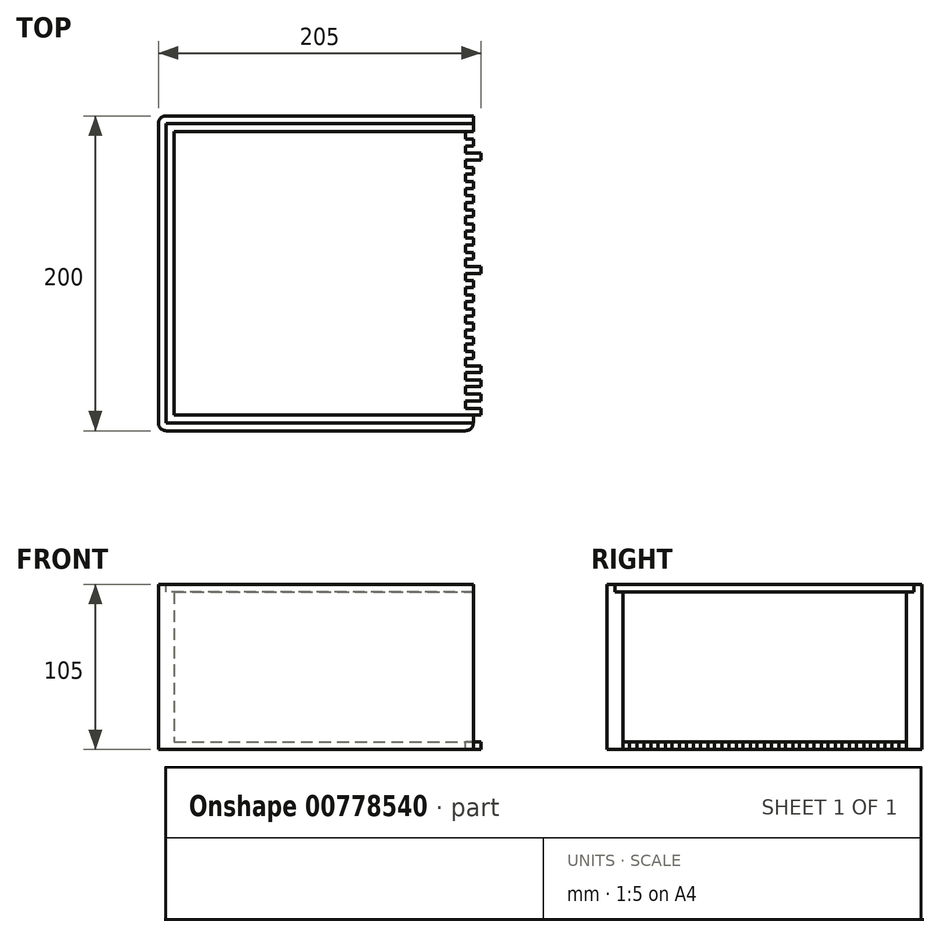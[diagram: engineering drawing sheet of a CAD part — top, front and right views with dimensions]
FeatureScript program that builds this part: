
annotation { "Feature Type Name" : "Feature", "Feature Type Description" : "" }
export const myFeature = defineFeature(function(context is Context, id is Id, definition is map)
    precondition{}
    {
        {
            var Q0;
            Q0=qCreatedBy(makeId("Top.planeOp"),FACE);
            var sketch = newSketch(context, id + "F0", { "sketchPlane" : qUnion([Q0])});
            skLineSegment(sketch, "E0.bottom", {"start": v(100, -100) * mm, "end": v(-100, -100) * mm});
            skLineSegment(sketch, "E0.top", {"start": v(100, 100) * mm, "end": v(-100, 100) * mm});
            skLineSegment(sketch, "E0.left", {"start": v(100, -100) * mm, "end": v(100, 100) * mm});
            skLineSegment(sketch, "E0.right", {"start": v(-100, -100) * mm, "end": v(-100, 100) * mm});
            skPoint(sketch, "E0.middle", {"position": v(0, 0) * mm});
            skSolve(sketch);
        }
        {
            var Q0;
            Q0 = qSketchRegion(id + "F0", true);
            extrude(context, id + "F1", {"entities" : qUnion([Q0]), "depth" : 5 * mm, "offsetDistance" : 25 * mm});
        }
        {
            var Q0;
            Q0=makeQuery(id+"F1.opExtrude","CAP_FACE",FACE,{"disambiguationData":[OSD([sQuery(id+"F0.wireOp",EDGE,"E0.bottom"),sQuery(id+"F0.wireOp",EDGE,"E0.top"),sQuery(id+"F0.wireOp",EDGE,"E0.left"),sQuery(id+"F0.wireOp",EDGE,"E0.right")])],"isStart":false});
            var sketch = newSketch(context, id + "F2", { "sketchPlane" : qUnion([Q0])});
            skLineSegment(sketch, "E1.bottom", {"start": v(-100, 100) * mm, "end": v(100, 100) * mm});
            skLineSegment(sketch, "E1.top", {"start": v(-100, 90) * mm, "end": v(100, 90) * mm});
            skLineSegment(sketch, "E1.left", {"start": v(-100, 100) * mm, "end": v(-100, 90) * mm});
            skLineSegment(sketch, "E1.right", {"start": v(100, 100) * mm, "end": v(100, 90) * mm});
            skLineSegment(sketch, "E2.bottom", {"start": v(-100, 100) * mm, "end": v(-90, 100) * mm});
            skLineSegment(sketch, "E2.top", {"start": v(-100, -100) * mm, "end": v(-90, -100) * mm});
            skLineSegment(sketch, "E2.left", {"start": v(-100, 100) * mm, "end": v(-100, -100) * mm});
            skLineSegment(sketch, "E2.right", {"start": v(-90, 100) * mm, "end": v(-90, -100) * mm});
            skLineSegment(sketch, "E3.bottom", {"start": v(-100, -100) * mm, "end": v(100, -100) * mm});
            skLineSegment(sketch, "E3.top", {"start": v(-100, -90) * mm, "end": v(100, -90) * mm});
            skLineSegment(sketch, "E3.left", {"start": v(-100, -100) * mm, "end": v(-100, -90) * mm});
            skLineSegment(sketch, "E3.right", {"start": v(100, -100) * mm, "end": v(100, -90) * mm});
            skSolve(sketch);
        }
        {
            var Q0;
            Q0 = qSketchRegion(id + "F2", true);
            extrude(context, id + "F3", {"entities" : qUnion([Q0]), "operationType" : NewBodyOperationType.ADD, "depth" : 100 * mm, "offsetDistance" : 25 * mm});
        }
        {
            var Q0;
            Q0=makeQuery(id+"F3.opExtrude","CAP_FACE",FACE,{"disambiguationData":[OSD([sQuery(id+"F2.wireOp",EDGE,"E1.bottom"),sQuery(id+"F2.wireOp",EDGE,"E1.top"),sQuery(id+"F2.wireOp",EDGE,"E1.right"),sQuery(id+"F2.wireOp",EDGE,"E2.bottom"),sQuery(id+"F2.wireOp",EDGE,"E2.left"),sQuery(id+"F2.wireOp",EDGE,"E2.right"),sQuery(id+"F2.wireOp",EDGE,"E3.bottom"),sQuery(id+"F2.wireOp",EDGE,"E3.top"),sQuery(id+"F2.wireOp",EDGE,"E3.left"),sQuery(id+"F2.wireOp",EDGE,"E3.right")])],"isStart":false});
            var sketch = newSketch(context, id + "F4", { "sketchPlane" : qUnion([Q0])});
            skLineSegment(sketch, "E4", {"start": v(100, 95) * mm, "end": v(-95, 95) * mm});
            skLineSegment(sketch, "E5", {"start": v(-95, 95) * mm, "end": v(-95, -95) * mm});
            skLineSegment(sketch, "E6", {"start": v(-95, -95) * mm, "end": v(100, -95) * mm});
            skSolve(sketch);
        }
        {
            var Q0;
            {var subQ4=sQuery(id+"F4.wireOp",EDGE,"E4");Q0=makeQuery(id+"F4.imprint","IMPRINT",FACE,{"disambiguationData":[TD([[makeQuery(id+"F4.imprint","IMPRINT",EDGE,{"derivedFrom":subQ4}),1.0]])]});}
            extrude(context, id + "F5", {"entities" : qUnion([Q0]), "operationType" : NewBodyOperationType.REMOVE, "oppositeDirection" : true, "depth" : 5 * mm, "offsetDistance" : 25 * mm});
        }
        {
            var Q0;
            Q0=makeQuery(id+"F1.opExtrude","CAP_FACE",FACE,{"disambiguationData":[OSD([sQuery(id+"F0.wireOp",EDGE,"E0.bottom"),sQuery(id+"F0.wireOp",EDGE,"E0.top"),sQuery(id+"F0.wireOp",EDGE,"E0.left"),sQuery(id+"F0.wireOp",EDGE,"E0.right")])],"isStart":false});
            var sketch = newSketch(context, id + "F6", { "sketchPlane" : qUnion([Q0])});
            skLineSegment(sketch, "E7", {"start": v(100, -90) * mm, "end": v(100, 90) * mm});
            skLineSegment(sketch, "E8.bottom", {"start": v(100, -90) * mm, "end": v(95, -90) * mm});
            skLineSegment(sketch, "E8.top", {"start": v(100, -85.7) * mm, "end": v(95, -85.7) * mm});
            skLineSegment(sketch, "E8.left", {"start": v(100, -90) * mm, "end": v(100, -85.7) * mm});
            skLineSegment(sketch, "E8.right", {"start": v(95, -90) * mm, "end": v(95, -85.7) * mm});
            skLineSegment(sketch, "E9.top", {"start": v(100, -81) * mm, "end": v(95, -81) * mm});
            skLineSegment(sketch, "E9.left", {"start": v(100, -85.7) * mm, "end": v(100, -81) * mm});
            skLineSegment(sketch, "E9.right", {"start": v(95, -85.7) * mm, "end": v(95, -81) * mm});
            skLineSegment(sketch, "E10.0.1.0", {"start": v(95, -81) * mm, "end": v(95, -76.7) * mm});
            skLineSegment(sketch, "E10.0.1.1", {"start": v(100, -81) * mm, "end": v(100, -76.7) * mm});
            skLineSegment(sketch, "E10.0.1.2", {"start": v(100, -76.7) * mm, "end": v(100, -72) * mm});
            skLineSegment(sketch, "E10.0.1.3", {"start": v(95, -76.7) * mm, "end": v(95, -72) * mm});
            skLineSegment(sketch, "E10.0.1.4", {"start": v(100, -76.7) * mm, "end": v(95, -76.7) * mm});
            skLineSegment(sketch, "E10.0.1.5", {"start": v(100, -72) * mm, "end": v(95, -72) * mm});
            skLineSegment(sketch, "E10.0.2.0", {"start": v(95, -72) * mm, "end": v(95, -67.7) * mm});
            skLineSegment(sketch, "E10.0.2.1", {"start": v(100, -72) * mm, "end": v(100, -67.7) * mm});
            skLineSegment(sketch, "E10.0.2.2", {"start": v(100, -67.7) * mm, "end": v(100, -63) * mm});
            skLineSegment(sketch, "E10.0.2.3", {"start": v(95, -67.7) * mm, "end": v(95, -63) * mm});
            skLineSegment(sketch, "E10.0.2.4", {"start": v(100, -67.7) * mm, "end": v(95, -67.7) * mm});
            skLineSegment(sketch, "E10.0.2.5", {"start": v(100, -63) * mm, "end": v(95, -63) * mm});
            skLineSegment(sketch, "E10.0.3.0", {"start": v(95, -63) * mm, "end": v(95, -58.7) * mm});
            skLineSegment(sketch, "E10.0.3.1", {"start": v(100, -63) * mm, "end": v(100, -58.7) * mm});
            skLineSegment(sketch, "E10.0.3.2", {"start": v(100, -58.7) * mm, "end": v(100, -54) * mm});
            skLineSegment(sketch, "E10.0.3.3", {"start": v(95, -58.7) * mm, "end": v(95, -54) * mm});
            skLineSegment(sketch, "E10.0.3.4", {"start": v(100, -58.7) * mm, "end": v(95, -58.7) * mm});
            skLineSegment(sketch, "E10.0.3.5", {"start": v(100, -54) * mm, "end": v(95, -54) * mm});
            skLineSegment(sketch, "E10.0.4.0", {"start": v(95, -54) * mm, "end": v(95, -49.7) * mm});
            skLineSegment(sketch, "E10.0.4.1", {"start": v(100, -54) * mm, "end": v(100, -49.7) * mm});
            skLineSegment(sketch, "E10.0.4.2", {"start": v(100, -49.7) * mm, "end": v(100, -45) * mm});
            skLineSegment(sketch, "E10.0.4.3", {"start": v(95, -49.7) * mm, "end": v(95, -45) * mm});
            skLineSegment(sketch, "E10.0.4.4", {"start": v(100, -49.7) * mm, "end": v(95, -49.7) * mm});
            skLineSegment(sketch, "E10.0.4.5", {"start": v(100, -45) * mm, "end": v(95, -45) * mm});
            skLineSegment(sketch, "E10.0.5.0", {"start": v(95, -45) * mm, "end": v(95, -40.7) * mm});
            skLineSegment(sketch, "E10.0.5.1", {"start": v(100, -45) * mm, "end": v(100, -40.7) * mm});
            skLineSegment(sketch, "E10.0.5.2", {"start": v(100, -40.7) * mm, "end": v(100, -36) * mm});
            skLineSegment(sketch, "E10.0.5.3", {"start": v(95, -40.7) * mm, "end": v(95, -36) * mm});
            skLineSegment(sketch, "E10.0.5.4", {"start": v(100, -40.7) * mm, "end": v(95, -40.7) * mm});
            skLineSegment(sketch, "E10.0.5.5", {"start": v(100, -36) * mm, "end": v(95, -36) * mm});
            skLineSegment(sketch, "E10.0.6.0", {"start": v(95, -36) * mm, "end": v(95, -31.7) * mm});
            skLineSegment(sketch, "E10.0.6.1", {"start": v(100, -36) * mm, "end": v(100, -31.7) * mm});
            skLineSegment(sketch, "E10.0.6.2", {"start": v(100, -31.7) * mm, "end": v(100, -27) * mm});
            skLineSegment(sketch, "E10.0.6.3", {"start": v(95, -31.7) * mm, "end": v(95, -27) * mm});
            skLineSegment(sketch, "E10.0.6.4", {"start": v(100, -31.7) * mm, "end": v(95, -31.7) * mm});
            skLineSegment(sketch, "E10.0.6.5", {"start": v(100, -27) * mm, "end": v(95, -27) * mm});
            skLineSegment(sketch, "E10.0.7.0", {"start": v(95, -27) * mm, "end": v(95, -22.7) * mm});
            skLineSegment(sketch, "E10.0.7.1", {"start": v(100, -27) * mm, "end": v(100, -22.7) * mm});
            skLineSegment(sketch, "E10.0.7.2", {"start": v(100, -22.7) * mm, "end": v(100, -18) * mm});
            skLineSegment(sketch, "E10.0.7.3", {"start": v(95, -22.7) * mm, "end": v(95, -18) * mm});
            skLineSegment(sketch, "E10.0.7.4", {"start": v(100, -22.7) * mm, "end": v(95, -22.7) * mm});
            skLineSegment(sketch, "E10.0.7.5", {"start": v(100, -18) * mm, "end": v(95, -18) * mm});
            skLineSegment(sketch, "E10.0.8.0", {"start": v(95, -18) * mm, "end": v(95, -13.7) * mm});
            skLineSegment(sketch, "E10.0.8.1", {"start": v(100, -18) * mm, "end": v(100, -13.7) * mm});
            skLineSegment(sketch, "E10.0.8.2", {"start": v(100, -13.7) * mm, "end": v(100, -9) * mm});
            skLineSegment(sketch, "E10.0.8.3", {"start": v(95, -13.7) * mm, "end": v(95, -9) * mm});
            skLineSegment(sketch, "E10.0.8.4", {"start": v(100, -13.7) * mm, "end": v(95, -13.7) * mm});
            skLineSegment(sketch, "E10.0.8.5", {"start": v(100, -9) * mm, "end": v(95, -9) * mm});
            skLineSegment(sketch, "E10.0.9.0", {"start": v(95, -9) * mm, "end": v(95, -4.7) * mm});
            skLineSegment(sketch, "E10.0.9.1", {"start": v(100, -9) * mm, "end": v(100, -4.7) * mm});
            skLineSegment(sketch, "E10.0.9.2", {"start": v(100, -4.7) * mm, "end": v(100, 0) * mm});
            skLineSegment(sketch, "E10.0.9.3", {"start": v(95, -4.7) * mm, "end": v(95, 0) * mm});
            skLineSegment(sketch, "E10.0.9.4", {"start": v(100, -4.7) * mm, "end": v(95, -4.7) * mm});
            skLineSegment(sketch, "E10.0.9.5", {"start": v(100, 0) * mm, "end": v(95, 0) * mm});
            skLineSegment(sketch, "E10.0.10.0", {"start": v(95, 0) * mm, "end": v(95, 4.3) * mm});
            skLineSegment(sketch, "E10.0.10.1", {"start": v(100, 0) * mm, "end": v(100, 4.3) * mm});
            skLineSegment(sketch, "E10.0.10.2", {"start": v(100, 4.3) * mm, "end": v(100, 9) * mm});
            skLineSegment(sketch, "E10.0.10.3", {"start": v(95, 4.3) * mm, "end": v(95, 9) * mm});
            skLineSegment(sketch, "E10.0.10.4", {"start": v(100, 4.3) * mm, "end": v(95, 4.3) * mm});
            skLineSegment(sketch, "E10.0.10.5", {"start": v(100, 9) * mm, "end": v(95, 9) * mm});
            skLineSegment(sketch, "E10.0.11.0", {"start": v(95, 9) * mm, "end": v(95, 13.3) * mm});
            skLineSegment(sketch, "E10.0.11.1", {"start": v(100, 9) * mm, "end": v(100, 13.3) * mm});
            skLineSegment(sketch, "E10.0.11.2", {"start": v(100, 13.3) * mm, "end": v(100, 18) * mm});
            skLineSegment(sketch, "E10.0.11.3", {"start": v(95, 13.3) * mm, "end": v(95, 18) * mm});
            skLineSegment(sketch, "E10.0.11.4", {"start": v(100, 13.3) * mm, "end": v(95, 13.3) * mm});
            skLineSegment(sketch, "E10.0.11.5", {"start": v(100, 18) * mm, "end": v(95, 18) * mm});
            skLineSegment(sketch, "E10.0.12.0", {"start": v(95, 18) * mm, "end": v(95, 22.3) * mm});
            skLineSegment(sketch, "E10.0.12.1", {"start": v(100, 18) * mm, "end": v(100, 22.3) * mm});
            skLineSegment(sketch, "E10.0.12.2", {"start": v(100, 22.3) * mm, "end": v(100, 27) * mm});
            skLineSegment(sketch, "E10.0.12.3", {"start": v(95, 22.3) * mm, "end": v(95, 27) * mm});
            skLineSegment(sketch, "E10.0.12.4", {"start": v(100, 22.3) * mm, "end": v(95, 22.3) * mm});
            skLineSegment(sketch, "E10.0.12.5", {"start": v(100, 27) * mm, "end": v(95, 27) * mm});
            skLineSegment(sketch, "E10.0.13.0", {"start": v(95, 27) * mm, "end": v(95, 31.3) * mm});
            skLineSegment(sketch, "E10.0.13.1", {"start": v(100, 27) * mm, "end": v(100, 31.3) * mm});
            skLineSegment(sketch, "E10.0.13.2", {"start": v(100, 31.3) * mm, "end": v(100, 36) * mm});
            skLineSegment(sketch, "E10.0.13.3", {"start": v(95, 31.3) * mm, "end": v(95, 36) * mm});
            skLineSegment(sketch, "E10.0.13.4", {"start": v(100, 31.3) * mm, "end": v(95, 31.3) * mm});
            skLineSegment(sketch, "E10.0.13.5", {"start": v(100, 36) * mm, "end": v(95, 36) * mm});
            skLineSegment(sketch, "E10.0.14.0", {"start": v(95, 36) * mm, "end": v(95, 40.3) * mm});
            skLineSegment(sketch, "E10.0.14.1", {"start": v(100, 36) * mm, "end": v(100, 40.3) * mm});
            skLineSegment(sketch, "E10.0.14.2", {"start": v(100, 40.3) * mm, "end": v(100, 45) * mm});
            skLineSegment(sketch, "E10.0.14.3", {"start": v(95, 40.3) * mm, "end": v(95, 45) * mm});
            skLineSegment(sketch, "E10.0.14.4", {"start": v(100, 40.3) * mm, "end": v(95, 40.3) * mm});
            skLineSegment(sketch, "E10.0.14.5", {"start": v(100, 45) * mm, "end": v(95, 45) * mm});
            skLineSegment(sketch, "E10.0.15.0", {"start": v(95, 45) * mm, "end": v(95, 49.3) * mm});
            skLineSegment(sketch, "E10.0.15.1", {"start": v(100, 45) * mm, "end": v(100, 49.3) * mm});
            skLineSegment(sketch, "E10.0.15.2", {"start": v(100, 49.3) * mm, "end": v(100, 54) * mm});
            skLineSegment(sketch, "E10.0.15.3", {"start": v(95, 49.3) * mm, "end": v(95, 54) * mm});
            skLineSegment(sketch, "E10.0.15.4", {"start": v(100, 49.3) * mm, "end": v(95, 49.3) * mm});
            skLineSegment(sketch, "E10.0.15.5", {"start": v(100, 54) * mm, "end": v(95, 54) * mm});
            skLineSegment(sketch, "E10.0.16.0", {"start": v(95, 54) * mm, "end": v(95, 58.3) * mm});
            skLineSegment(sketch, "E10.0.16.1", {"start": v(100, 54) * mm, "end": v(100, 58.3) * mm});
            skLineSegment(sketch, "E10.0.16.2", {"start": v(100, 58.3) * mm, "end": v(100, 63) * mm});
            skLineSegment(sketch, "E10.0.16.3", {"start": v(95, 58.3) * mm, "end": v(95, 63) * mm});
            skLineSegment(sketch, "E10.0.16.4", {"start": v(100, 58.3) * mm, "end": v(95, 58.3) * mm});
            skLineSegment(sketch, "E10.0.16.5", {"start": v(100, 63) * mm, "end": v(95, 63) * mm});
            skLineSegment(sketch, "E10.0.17.0", {"start": v(95, 63) * mm, "end": v(95, 67.3) * mm});
            skLineSegment(sketch, "E10.0.17.1", {"start": v(100, 63) * mm, "end": v(100, 67.3) * mm});
            skLineSegment(sketch, "E10.0.17.2", {"start": v(100, 67.3) * mm, "end": v(100, 72) * mm});
            skLineSegment(sketch, "E10.0.17.3", {"start": v(95, 67.3) * mm, "end": v(95, 72) * mm});
            skLineSegment(sketch, "E10.0.17.4", {"start": v(100, 67.3) * mm, "end": v(95, 67.3) * mm});
            skLineSegment(sketch, "E10.0.17.5", {"start": v(100, 72) * mm, "end": v(95, 72) * mm});
            skLineSegment(sketch, "E10.0.18.0", {"start": v(95, 72) * mm, "end": v(95, 76.3) * mm});
            skLineSegment(sketch, "E10.0.18.1", {"start": v(100, 72) * mm, "end": v(100, 76.3) * mm});
            skLineSegment(sketch, "E10.0.18.2", {"start": v(100, 76.3) * mm, "end": v(100, 81) * mm});
            skLineSegment(sketch, "E10.0.18.3", {"start": v(95, 76.3) * mm, "end": v(95, 81) * mm});
            skLineSegment(sketch, "E10.0.18.4", {"start": v(100, 76.3) * mm, "end": v(95, 76.3) * mm});
            skLineSegment(sketch, "E10.0.18.5", {"start": v(100, 81) * mm, "end": v(95, 81) * mm});
            skLineSegment(sketch, "E10.0.19.0", {"start": v(95, 81) * mm, "end": v(95, 85.3) * mm});
            skLineSegment(sketch, "E10.0.19.1", {"start": v(100, 81) * mm, "end": v(100, 85.3) * mm});
            skLineSegment(sketch, "E10.0.19.2", {"start": v(100, 85.3) * mm, "end": v(100, 90) * mm});
            skLineSegment(sketch, "E10.0.19.3", {"start": v(95, 85.3) * mm, "end": v(95, 90) * mm});
            skLineSegment(sketch, "E10.0.19.4", {"start": v(100, 85.3) * mm, "end": v(95, 85.3) * mm});
            skLineSegment(sketch, "E10.0.19.5", {"start": v(100, 90) * mm, "end": v(95, 90) * mm});
            skLineSegment(sketch, "E10.direction1", {"start": v(95, -90) * mm, "end": v(120, -90) * mm, "construction": true});
            skLineSegment(sketch, "E10.direction2", {"start": v(95, -90) * mm, "end": v(95, -81) * mm, "construction": true});
            skLineSegment(sketch, "E11.MirrorCS", {"start": v(105, 72) * mm, "end": v(105, 76.3) * mm});
            skLineSegment(sketch, "E12.MirrorCS", {"start": v(105, -13.7) * mm, "end": v(105, -9) * mm});
            skLineSegment(sketch, "E13.MirrorCS", {"start": v(105, 0) * mm, "end": v(105, 4.3) * mm});
            skLineSegment(sketch, "E14.MirrorCS", {"start": v(105, 81) * mm, "end": v(105, 85.3) * mm});
            skLineSegment(sketch, "E15.MirrorCS", {"start": v(105, 9) * mm, "end": v(105, 13.3) * mm});
            skLineSegment(sketch, "E16.MirrorCS", {"start": v(105, 22.3) * mm, "end": v(105, 27) * mm});
            skLineSegment(sketch, "E17.MirrorCS", {"start": v(105, -4.7) * mm, "end": v(105, 0) * mm});
            skLineSegment(sketch, "E18.MirrorCS", {"start": v(105, -27) * mm, "end": v(105, -22.7) * mm});
            skLineSegment(sketch, "E19.MirrorCS", {"start": v(105, 45) * mm, "end": v(105, 49.3) * mm});
            skLineSegment(sketch, "E20.MirrorCS", {"start": v(105, -40.7) * mm, "end": v(105, -36) * mm});
            skLineSegment(sketch, "E21.MirrorCS", {"start": v(105, 18) * mm, "end": v(105, 22.3) * mm});
            skLineSegment(sketch, "E22.MirrorCS", {"start": v(105, -18) * mm, "end": v(105, -13.7) * mm});
            skLineSegment(sketch, "E23.MirrorCS", {"start": v(105, 54) * mm, "end": v(105, 58.3) * mm});
            skLineSegment(sketch, "E24.MirrorCS", {"start": v(105, -31.7) * mm, "end": v(105, -27) * mm});
            skLineSegment(sketch, "E25.MirrorCS", {"start": v(105, 63) * mm, "end": v(105, 67.3) * mm});
            skLineSegment(sketch, "E26.MirrorCS", {"start": v(105, -9) * mm, "end": v(105, -4.7) * mm});
            skLineSegment(sketch, "E27.MirrorCS", {"start": v(105, 76.3) * mm, "end": v(105, 81) * mm});
            skLineSegment(sketch, "E28.MirrorCS", {"start": v(105, 13.3) * mm, "end": v(105, 18) * mm});
            skLineSegment(sketch, "E29.MirrorCS", {"start": v(105, 27) * mm, "end": v(105, 31.3) * mm});
            skLineSegment(sketch, "E30.MirrorCS", {"start": v(105, -45) * mm, "end": v(105, -40.7) * mm});
            skLineSegment(sketch, "E31.MirrorCS", {"start": v(105, 36) * mm, "end": v(105, 40.3) * mm});
            skLineSegment(sketch, "E32.MirrorCS", {"start": v(105, -36) * mm, "end": v(105, -31.7) * mm});
            skLineSegment(sketch, "E33.MirrorCS", {"start": v(105, 49.3) * mm, "end": v(105, 54) * mm});
            skLineSegment(sketch, "E34.MirrorCS", {"start": v(100, 22.3) * mm, "end": v(105, 22.3) * mm});
            skLineSegment(sketch, "E35.MirrorCS", {"start": v(100, 36) * mm, "end": v(105, 36) * mm});
            skLineSegment(sketch, "E36.MirrorCS", {"start": v(105, 58.3) * mm, "end": v(105, 63) * mm});
            skLineSegment(sketch, "E37.MirrorCS", {"start": v(100, -49.7) * mm, "end": v(105, -49.7) * mm});
            skLineSegment(sketch, "E38.MirrorCS", {"start": v(100, -36) * mm, "end": v(105, -36) * mm});
            skLineSegment(sketch, "E39.MirrorCS", {"start": v(100, 72) * mm, "end": v(105, 72) * mm});
            skLineSegment(sketch, "E40.MirrorCS", {"start": v(100, 0) * mm, "end": v(105, 0) * mm});
            skLineSegment(sketch, "E41.MirrorCS", {"start": v(100, 31.3) * mm, "end": v(105, 31.3) * mm});
            skLineSegment(sketch, "E42.MirrorCS", {"start": v(100, -40.7) * mm, "end": v(105, -40.7) * mm});
            skLineSegment(sketch, "E43.MirrorCS", {"start": v(105, -49.7) * mm, "end": v(105, -45) * mm});
            skLineSegment(sketch, "E44.MirrorCS", {"start": v(100, 45) * mm, "end": v(105, 45) * mm});
            skLineSegment(sketch, "E45.MirrorCS", {"start": v(105, 67.3) * mm, "end": v(105, 72) * mm});
            skLineSegment(sketch, "E46.MirrorCS", {"start": v(100, -27) * mm, "end": v(105, -27) * mm});
            skLineSegment(sketch, "E47.MirrorCS", {"start": v(100, 81) * mm, "end": v(105, 81) * mm});
            skLineSegment(sketch, "E48.MirrorCS", {"start": v(100, 67.3) * mm, "end": v(105, 67.3) * mm});
            skLineSegment(sketch, "E49.MirrorCS", {"start": v(100, 9) * mm, "end": v(105, 9) * mm});
            skLineSegment(sketch, "E50.MirrorCS", {"start": v(100, -4.7) * mm, "end": v(105, -4.7) * mm});
            skLineSegment(sketch, "E51.MirrorCS", {"start": v(105, 31.3) * mm, "end": v(105, 36) * mm});
            skLineSegment(sketch, "E52.MirrorCS", {"start": v(100, 40.3) * mm, "end": v(105, 40.3) * mm});
            skLineSegment(sketch, "E53.MirrorCS", {"start": v(100, -31.7) * mm, "end": v(105, -31.7) * mm});
            skLineSegment(sketch, "E54.MirrorCS", {"start": v(100, 4.3) * mm, "end": v(105, 4.3) * mm});
            skLineSegment(sketch, "E55.MirrorCS", {"start": v(105, 40.3) * mm, "end": v(105, 45) * mm});
            skLineSegment(sketch, "E56.MirrorCS", {"start": v(100, 90) * mm, "end": v(105, 90) * mm});
            skLineSegment(sketch, "E57.MirrorCS", {"start": v(100, 18) * mm, "end": v(105, 18) * mm});
            skLineSegment(sketch, "E58.MirrorCS", {"start": v(100, 76.3) * mm, "end": v(105, 76.3) * mm});
            skLineSegment(sketch, "E59.MirrorCS", {"start": v(100, 85.3) * mm, "end": v(105, 85.3) * mm});
            skLineSegment(sketch, "E60.MirrorCS", {"start": v(100, 13.3) * mm, "end": v(105, 13.3) * mm});
            skLineSegment(sketch, "E61.MirrorCS", {"start": v(100, -18) * mm, "end": v(105, -18) * mm});
            skLineSegment(sketch, "E62.MirrorCS", {"start": v(105, 4.3) * mm, "end": v(105, 9) * mm});
            skLineSegment(sketch, "E63.MirrorCS", {"start": v(100, 54) * mm, "end": v(105, 54) * mm});
            skLineSegment(sketch, "E64.MirrorCS", {"start": v(100, 63) * mm, "end": v(105, 63) * mm});
            skLineSegment(sketch, "E65.MirrorCS", {"start": v(105, 85.3) * mm, "end": v(105, 90) * mm});
            skLineSegment(sketch, "E66.MirrorCS", {"start": v(100, -9) * mm, "end": v(105, -9) * mm});
            skLineSegment(sketch, "E67.MirrorCS", {"start": v(100, -22.7) * mm, "end": v(105, -22.7) * mm});
            skLineSegment(sketch, "E68.MirrorCS", {"start": v(100, 49.3) * mm, "end": v(105, 49.3) * mm});
            skLineSegment(sketch, "E69.MirrorCS", {"start": v(100, 58.3) * mm, "end": v(105, 58.3) * mm});
            skLineSegment(sketch, "E70.MirrorCS", {"start": v(100, -13.7) * mm, "end": v(105, -13.7) * mm});
            skLineSegment(sketch, "E71.MirrorCS", {"start": v(100, -45) * mm, "end": v(105, -45) * mm});
            skLineSegment(sketch, "E72.MirrorCS", {"start": v(105, -22.7) * mm, "end": v(105, -18) * mm});
            skLineSegment(sketch, "E73.MirrorCS", {"start": v(100, 27) * mm, "end": v(105, 27) * mm});
            skLineSegment(sketch, "E74.MirrorCS", {"start": v(105, -85.7) * mm, "end": v(105, -81) * mm});
            skLineSegment(sketch, "E75.MirrorCS", {"start": v(105, -90) * mm, "end": v(105, -85.7) * mm});
            skLineSegment(sketch, "E76.MirrorCS", {"start": v(105, -90) * mm, "end": v(105, -81) * mm, "construction": true});
            skLineSegment(sketch, "E77.MirrorCS", {"start": v(105, -72) * mm, "end": v(105, -67.7) * mm});
            skLineSegment(sketch, "E78.MirrorCS", {"start": v(105, -54) * mm, "end": v(105, -49.7) * mm});
            skLineSegment(sketch, "E79.MirrorCS", {"start": v(105, -81) * mm, "end": v(105, -76.7) * mm});
            skLineSegment(sketch, "E80.MirrorCS", {"start": v(105, -63) * mm, "end": v(105, -58.7) * mm});
            skLineSegment(sketch, "E81.MirrorCS", {"start": v(105, -67.7) * mm, "end": v(105, -63) * mm});
            skLineSegment(sketch, "E82.MirrorCS", {"start": v(105, -58.7) * mm, "end": v(105, -54) * mm});
            skLineSegment(sketch, "E83.MirrorCS", {"start": v(100, -85.7) * mm, "end": v(105, -85.7) * mm});
            skLineSegment(sketch, "E84.MirrorCS", {"start": v(100, -81) * mm, "end": v(105, -81) * mm});
            skLineSegment(sketch, "E85.MirrorCS", {"start": v(100, -90) * mm, "end": v(105, -90) * mm});
            skLineSegment(sketch, "E86.MirrorCS", {"start": v(100, -72) * mm, "end": v(105, -72) * mm});
            skLineSegment(sketch, "E87.MirrorCS", {"start": v(100, -76.7) * mm, "end": v(105, -76.7) * mm});
            skLineSegment(sketch, "E88.MirrorCS", {"start": v(100, -54) * mm, "end": v(105, -54) * mm});
            skLineSegment(sketch, "E89.MirrorCS", {"start": v(100, -58.7) * mm, "end": v(105, -58.7) * mm});
            skLineSegment(sketch, "E90.MirrorCS", {"start": v(105, -76.7) * mm, "end": v(105, -72) * mm});
            skLineSegment(sketch, "E91.MirrorCS", {"start": v(100, -63) * mm, "end": v(105, -63) * mm});
            skLineSegment(sketch, "E92.MirrorCS", {"start": v(100, -67.7) * mm, "end": v(105, -67.7) * mm});
            skSolve(sketch);
        }
        {
            var Q0;
            Q0=makeQuery(id+"F6.imprint","IMPRINT",FACE,{"disambiguationData":[TD([[makeQuery(id+"F6.imprint","IMPRINT",EDGE,{"derivedFrom":sQuery(id+"F6.wireOp",EDGE,"E8.top")}),-1.0]])]});
            var Q1;
            Q1=makeQuery(id+"F6.imprint","IMPRINT",FACE,{"disambiguationData":[TD([[makeQuery(id+"F6.imprint","IMPRINT",EDGE,{"derivedFrom":sQuery(id+"F6.wireOp",EDGE,"E10.0.1.3")}),-1.0]])]});
            var Q2;
            Q2=makeQuery(id+"F6.imprint","IMPRINT",FACE,{"disambiguationData":[TD([[makeQuery(id+"F6.imprint","IMPRINT",EDGE,{"derivedFrom":sQuery(id+"F6.wireOp",EDGE,"E10.0.2.3")}),-1.0]])]});
            var Q3;
            Q3=makeQuery(id+"F6.imprint","IMPRINT",FACE,{"disambiguationData":[TD([[makeQuery(id+"F6.imprint","IMPRINT",EDGE,{"derivedFrom":sQuery(id+"F6.wireOp",EDGE,"E10.0.3.3")}),-1.0]])]});
            var Q4;
            Q4=makeQuery(id+"F6.imprint","IMPRINT",FACE,{"disambiguationData":[TD([[makeQuery(id+"F6.imprint","IMPRINT",EDGE,{"derivedFrom":sQuery(id+"F6.wireOp",EDGE,"E10.0.4.3")}),-1.0]])]});
            var Q5;
            Q5=makeQuery(id+"F6.imprint","IMPRINT",FACE,{"disambiguationData":[TD([[makeQuery(id+"F6.imprint","IMPRINT",EDGE,{"derivedFrom":sQuery(id+"F6.wireOp",EDGE,"E10.0.5.3")}),-1.0]])]});
            var Q6;
            Q6=makeQuery(id+"F6.imprint","IMPRINT",FACE,{"disambiguationData":[TD([[makeQuery(id+"F6.imprint","IMPRINT",EDGE,{"derivedFrom":sQuery(id+"F6.wireOp",EDGE,"E10.0.6.3")}),-1.0]])]});
            var Q7;
            Q7=makeQuery(id+"F6.imprint","IMPRINT",FACE,{"disambiguationData":[TD([[makeQuery(id+"F6.imprint","IMPRINT",EDGE,{"derivedFrom":sQuery(id+"F6.wireOp",EDGE,"E10.0.7.3")}),-1.0]])]});
            var Q8;
            Q8=makeQuery(id+"F6.imprint","IMPRINT",FACE,{"disambiguationData":[TD([[makeQuery(id+"F6.imprint","IMPRINT",EDGE,{"derivedFrom":sQuery(id+"F6.wireOp",EDGE,"E10.0.8.3")}),-1.0]])]});
            var Q9;
            Q9=makeQuery(id+"F6.imprint","IMPRINT",FACE,{"disambiguationData":[TD([[makeQuery(id+"F6.imprint","IMPRINT",EDGE,{"derivedFrom":sQuery(id+"F6.wireOp",EDGE,"E10.0.9.3")}),-1.0]])]});
            var Q10;
            Q10=makeQuery(id+"F6.imprint","IMPRINT",FACE,{"disambiguationData":[TD([[makeQuery(id+"F6.imprint","IMPRINT",EDGE,{"derivedFrom":sQuery(id+"F6.wireOp",EDGE,"E10.0.10.3")}),-1.0]])]});
            var Q11;
            Q11=makeQuery(id+"F6.imprint","IMPRINT",FACE,{"disambiguationData":[TD([[makeQuery(id+"F6.imprint","IMPRINT",EDGE,{"derivedFrom":sQuery(id+"F6.wireOp",EDGE,"E10.0.11.3")}),-1.0]])]});
            var Q12;
            Q12=makeQuery(id+"F6.imprint","IMPRINT",FACE,{"disambiguationData":[TD([[makeQuery(id+"F6.imprint","IMPRINT",EDGE,{"derivedFrom":sQuery(id+"F6.wireOp",EDGE,"E10.0.12.3")}),-1.0]])]});
            var Q13;
            Q13=makeQuery(id+"F6.imprint","IMPRINT",FACE,{"disambiguationData":[TD([[makeQuery(id+"F6.imprint","IMPRINT",EDGE,{"derivedFrom":sQuery(id+"F6.wireOp",EDGE,"E10.0.13.3")}),-1.0]])]});
            var Q14;
            Q14=makeQuery(id+"F6.imprint","IMPRINT",FACE,{"disambiguationData":[TD([[makeQuery(id+"F6.imprint","IMPRINT",EDGE,{"derivedFrom":sQuery(id+"F6.wireOp",EDGE,"E10.0.14.3")}),-1.0]])]});
            var Q15;
            Q15=makeQuery(id+"F6.imprint","IMPRINT",FACE,{"disambiguationData":[TD([[makeQuery(id+"F6.imprint","IMPRINT",EDGE,{"derivedFrom":sQuery(id+"F6.wireOp",EDGE,"E10.0.15.3")}),-1.0]])]});
            var Q16;
            Q16=makeQuery(id+"F6.imprint","IMPRINT",FACE,{"disambiguationData":[TD([[makeQuery(id+"F6.imprint","IMPRINT",EDGE,{"derivedFrom":sQuery(id+"F6.wireOp",EDGE,"E10.0.16.3")}),-1.0]])]});
            var Q17;
            Q17=makeQuery(id+"F6.imprint","IMPRINT",FACE,{"disambiguationData":[TD([[makeQuery(id+"F6.imprint","IMPRINT",EDGE,{"derivedFrom":sQuery(id+"F6.wireOp",EDGE,"E10.0.17.3")}),-1.0]])]});
            var Q18;
            Q18=makeQuery(id+"F6.imprint","IMPRINT",FACE,{"disambiguationData":[TD([[makeQuery(id+"F6.imprint","IMPRINT",EDGE,{"derivedFrom":sQuery(id+"F6.wireOp",EDGE,"E10.0.18.3")}),-1.0]])]});
            var Q19;
            Q19=makeQuery(id+"F6.imprint","IMPRINT",FACE,{"disambiguationData":[TD([[makeQuery(id+"F6.imprint","IMPRINT",EDGE,{"derivedFrom":sQuery(id+"F6.wireOp",EDGE,"E10.0.19.3")}),-1.0]])]});
            extrude(context, id + "F7", {"entities" : qUnion([Q0, Q1, Q2, Q3, Q4, Q5, Q6, Q7, Q8, Q9, Q10, Q11, Q12, Q13, Q14, Q15, Q16, Q17, Q18, Q19]), "operationType" : NewBodyOperationType.REMOVE, "oppositeDirection" : true, "depth" : 25 * mm, "offsetDistance" : 25 * mm});
        }
        {
            var Q0;
            Q0=makeQuery(id+"F6.imprint","IMPRINT",FACE,{"disambiguationData":[TD([[makeQuery(id+"F6.imprint","IMPRINT",EDGE,{"derivedFrom":sQuery(id+"F6.wireOp",EDGE,"E75.MirrorCS")}),1.0]])]});
            var Q1;
            Q1=makeQuery(id+"F6.imprint","IMPRINT",FACE,{"disambiguationData":[TD([[makeQuery(id+"F6.imprint","IMPRINT",EDGE,{"derivedFrom":sQuery(id+"F6.wireOp",EDGE,"E79.MirrorCS")}),1.0]])]});
            var Q2;
            Q2=makeQuery(id+"F6.imprint","IMPRINT",FACE,{"disambiguationData":[TD([[makeQuery(id+"F6.imprint","IMPRINT",EDGE,{"derivedFrom":sQuery(id+"F6.wireOp",EDGE,"E77.MirrorCS")}),1.0]])]});
            var Q3;
            Q3=makeQuery(id+"F6.imprint","IMPRINT",FACE,{"disambiguationData":[TD([[makeQuery(id+"F6.imprint","IMPRINT",EDGE,{"derivedFrom":sQuery(id+"F6.wireOp",EDGE,"E80.MirrorCS")}),1.0]])]});
            var Q4;
            Q4=makeQuery(id+"F6.imprint","IMPRINT",FACE,{"disambiguationData":[TD([[makeQuery(id+"F6.imprint","IMPRINT",EDGE,{"derivedFrom":sQuery(id+"F6.wireOp",EDGE,"E10.0.4.1")}),-1.0]])]});
            var Q5;
            Q5=makeQuery(id+"F6.imprint","IMPRINT",FACE,{"disambiguationData":[TD([[makeQuery(id+"F6.imprint","IMPRINT",EDGE,{"derivedFrom":sQuery(id+"F6.wireOp",EDGE,"E10.0.5.1")}),-1.0]])]});
            var Q6;
            Q6=makeQuery(id+"F6.imprint","IMPRINT",FACE,{"disambiguationData":[TD([[makeQuery(id+"F6.imprint","IMPRINT",EDGE,{"derivedFrom":sQuery(id+"F6.wireOp",EDGE,"E10.0.6.1")}),-1.0]])]});
            var Q7;
            Q7=makeQuery(id+"F6.imprint","IMPRINT",FACE,{"disambiguationData":[TD([[makeQuery(id+"F6.imprint","IMPRINT",EDGE,{"derivedFrom":sQuery(id+"F6.wireOp",EDGE,"E10.0.7.1")}),-1.0]])]});
            var Q8;
            Q8=makeQuery(id+"F6.imprint","IMPRINT",FACE,{"disambiguationData":[TD([[makeQuery(id+"F6.imprint","IMPRINT",EDGE,{"derivedFrom":sQuery(id+"F6.wireOp",EDGE,"E10.0.8.1")}),-1.0]])]});
            var Q9;
            Q9=makeQuery(id+"F6.imprint","IMPRINT",FACE,{"disambiguationData":[TD([[makeQuery(id+"F6.imprint","IMPRINT",EDGE,{"derivedFrom":sQuery(id+"F6.wireOp",EDGE,"E10.0.9.1")}),-1.0]])]});
            var Q10;
            Q10=makeQuery(id+"F6.imprint","IMPRINT",FACE,{"disambiguationData":[TD([[makeQuery(id+"F6.imprint","IMPRINT",EDGE,{"derivedFrom":sQuery(id+"F6.wireOp",EDGE,"E13.MirrorCS")}),1.0]])]});
            var Q11;
            Q11=makeQuery(id+"F6.imprint","IMPRINT",FACE,{"disambiguationData":[TD([[makeQuery(id+"F6.imprint","IMPRINT",EDGE,{"derivedFrom":sQuery(id+"F6.wireOp",EDGE,"E10.0.11.1")}),-1.0]])]});
            var Q12;
            Q12=makeQuery(id+"F6.imprint","IMPRINT",FACE,{"disambiguationData":[TD([[makeQuery(id+"F6.imprint","IMPRINT",EDGE,{"derivedFrom":sQuery(id+"F6.wireOp",EDGE,"E10.0.12.1")}),-1.0]])]});
            var Q13;
            Q13=makeQuery(id+"F6.imprint","IMPRINT",FACE,{"disambiguationData":[TD([[makeQuery(id+"F6.imprint","IMPRINT",EDGE,{"derivedFrom":sQuery(id+"F6.wireOp",EDGE,"E10.0.13.1")}),-1.0]])]});
            var Q14;
            Q14=makeQuery(id+"F6.imprint","IMPRINT",FACE,{"disambiguationData":[TD([[makeQuery(id+"F6.imprint","IMPRINT",EDGE,{"derivedFrom":sQuery(id+"F6.wireOp",EDGE,"E10.0.14.1")}),-1.0]])]});
            var Q15;
            Q15=makeQuery(id+"F6.imprint","IMPRINT",FACE,{"disambiguationData":[TD([[makeQuery(id+"F6.imprint","IMPRINT",EDGE,{"derivedFrom":sQuery(id+"F6.wireOp",EDGE,"E10.0.15.1")}),-1.0]])]});
            var Q16;
            Q16=makeQuery(id+"F6.imprint","IMPRINT",FACE,{"disambiguationData":[TD([[makeQuery(id+"F6.imprint","IMPRINT",EDGE,{"derivedFrom":sQuery(id+"F6.wireOp",EDGE,"E10.0.16.1")}),-1.0]])]});
            var Q17;
            Q17=makeQuery(id+"F6.imprint","IMPRINT",FACE,{"disambiguationData":[TD([[makeQuery(id+"F6.imprint","IMPRINT",EDGE,{"derivedFrom":sQuery(id+"F6.wireOp",EDGE,"E10.0.17.1")}),-1.0]])]});
            var Q18;
            Q18=makeQuery(id+"F6.imprint","IMPRINT",FACE,{"disambiguationData":[TD([[makeQuery(id+"F6.imprint","IMPRINT",EDGE,{"derivedFrom":sQuery(id+"F6.wireOp",EDGE,"E11.MirrorCS")}),1.0]])]});
            var Q19;
            Q19=makeQuery(id+"F6.imprint","IMPRINT",FACE,{"disambiguationData":[TD([[makeQuery(id+"F6.imprint","IMPRINT",EDGE,{"derivedFrom":sQuery(id+"F6.wireOp",EDGE,"E10.0.19.1")}),-1.0]])]});
            extrude(context, id + "F8", {"entities" : qUnion([Q0, Q1, Q2, Q3, Q4, Q5, Q6, Q7, Q8, Q9, Q10, Q11, Q12, Q13, Q14, Q15, Q16, Q17, Q18, Q19]), "operationType" : NewBodyOperationType.ADD, "oppositeDirection" : true, "depth" : 5 * mm, "offsetDistance" : 25 * mm});
        }
        {
            var Q0;
            Q0=makeQuery(id+"F3.boolean.opBoolean","MERGE",EDGE,{"derivedFrom":[makeQuery(id+"F1.opExtrude","SWEPT_EDGE",EDGE,{"disambiguationData":[OSD([sQuery(id+"F0.wireOp",EDGE,"E0.bottom"),sQuery(id+"F0.wireOp",EDGE,"E0.right")])]}),makeQuery(id+"F3.opExtrude","SWEPT_EDGE",EDGE,{"disambiguationData":[OSD([sQuery(id+"F2.wireOp",EDGE,"E3.bottom"),sQuery(id+"F2.wireOp",EDGE,"E3.left")])]})]});
            var Q1;
            Q1=makeQuery(id+"F3.boolean.opBoolean","MERGE",EDGE,{"derivedFrom":[makeQuery(id+"F1.opExtrude","SWEPT_EDGE",EDGE,{"disambiguationData":[OSD([sQuery(id+"F0.wireOp",EDGE,"E0.top"),sQuery(id+"F0.wireOp",EDGE,"E0.right")])]}),makeQuery(id+"F3.opExtrude","SWEPT_EDGE",EDGE,{"disambiguationData":[OSD([sQuery(id+"F2.wireOp",EDGE,"E2.bottom"),sQuery(id+"F2.wireOp",EDGE,"E2.left")])]})]});
            fillet(context, id + "F9", {"entities" : qUnion([Q0, Q1]), "radius" : 5 * mm, "tangentPropagation" : true, "allowEdgeOverflow" : false});
        }
    });
